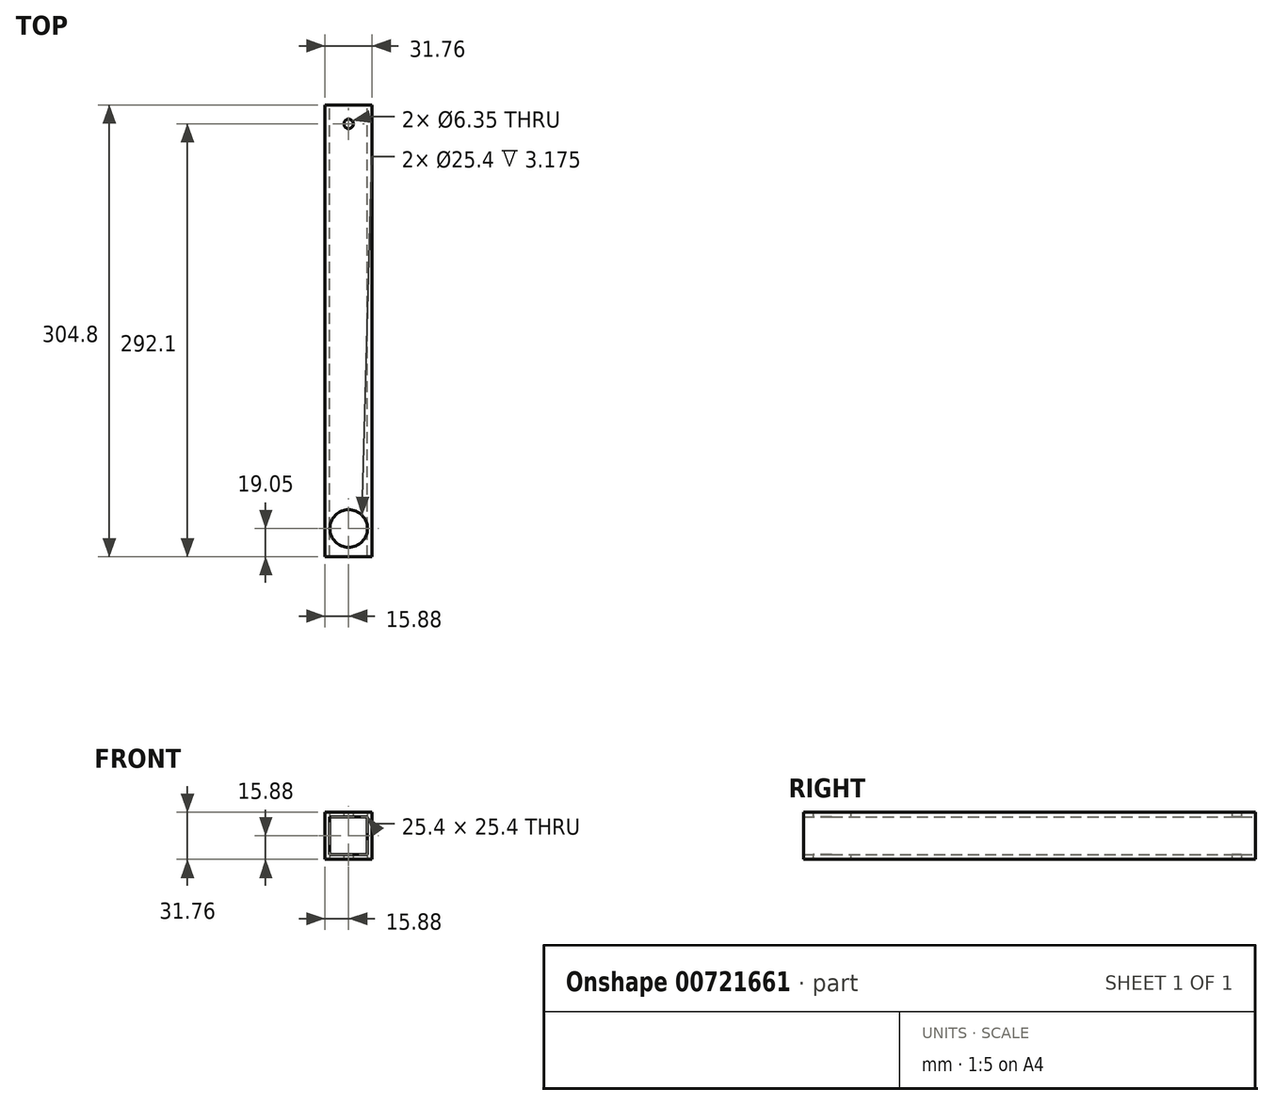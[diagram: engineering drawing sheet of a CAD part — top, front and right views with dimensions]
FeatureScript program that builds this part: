
annotation { "Feature Type Name" : "Feature", "Feature Type Description" : "" }
export const myFeature = defineFeature(function(context is Context, id is Id, definition is map)
    precondition{}
    {
        {
            var Q0;
            Q0=qCreatedBy(makeId("Front.planeOp"),FACE);
            var sketch = newSketch(context, id + "F0", { "sketchPlane" : qUnion([Q0])});
            skLineSegment(sketch, "E0.bottom", {"start": v(12.7, 12.7) * mm, "end": v(-12.7, 12.7) * mm});
            skLineSegment(sketch, "E0.top", {"start": v(12.7, -12.7) * mm, "end": v(-12.7, -12.7) * mm});
            skLineSegment(sketch, "E0.left", {"start": v(12.7, 12.7) * mm, "end": v(12.7, -12.7) * mm});
            skLineSegment(sketch, "E0.right", {"start": v(-12.7, 12.7) * mm, "end": v(-12.7, -12.7) * mm});
            skPoint(sketch, "E0.middle", {"position": v(0, 0) * mm});
            skLineSegment(sketch, "E1.0", {"start": v(15.88, -15.88) * mm, "end": v(-15.88, -15.88) * mm});
            skLineSegment(sketch, "E1.1", {"start": v(15.88, 15.88) * mm, "end": v(15.88, -15.88) * mm});
            skLineSegment(sketch, "E1.2", {"start": v(15.88, 15.88) * mm, "end": v(-15.88, 15.88) * mm});
            skLineSegment(sketch, "E1.3", {"start": v(-15.88, 15.88) * mm, "end": v(-15.88, -15.88) * mm});
            skSolve(sketch);
        }
        {
            var Q0;
            Q0 = qSketchRegion(id + "F0", true);
            extrude(context, id + "F1", {"entities" : qUnion([Q0]), "depth" : 304.8 * mm, "offsetDistance" : 25.4 * mm});
        }
        {
            var Q0;
            Q0=makeQuery(id+"F1.opExtrude","SWEPT_FACE",FACE,{"disambiguationData":[OSD([sQuery(id+"F0.wireOp",EDGE,"E1.0")])]});
            var sketch = newSketch(context, id + "F2", { "sketchPlane" : qUnion([Q0])});
            skLineSegment(sketch, "E2", {"start": v(0, 304.8) * mm, "end": v(0, 191.13) * mm, "construction": true});
            skCircle(sketch, "E3", {"center": v(0, 285.75) * mm, "radius": 12.7 * mm});
            skLineSegment(sketch, "E4", {"start": v(0, 0) * mm, "end": v(0, 70.34) * mm});
            skCircle(sketch, "E5", {"center": v(0, 12.7) * mm, "radius": 3.18 * mm});
            skSolve(sketch);
        }
        {
            var Q0;
            Q0 = qSketchRegion(id + "F2", true);
            extrude(context, id + "F3", {"entities" : qUnion([Q0]), "operationType" : NewBodyOperationType.REMOVE, "endBound" : BoundingType.THROUGH_ALL, "oppositeDirection" : true, "depth" : 25.4 * mm, "offsetDistance" : 25.4 * mm});
        }
    });
